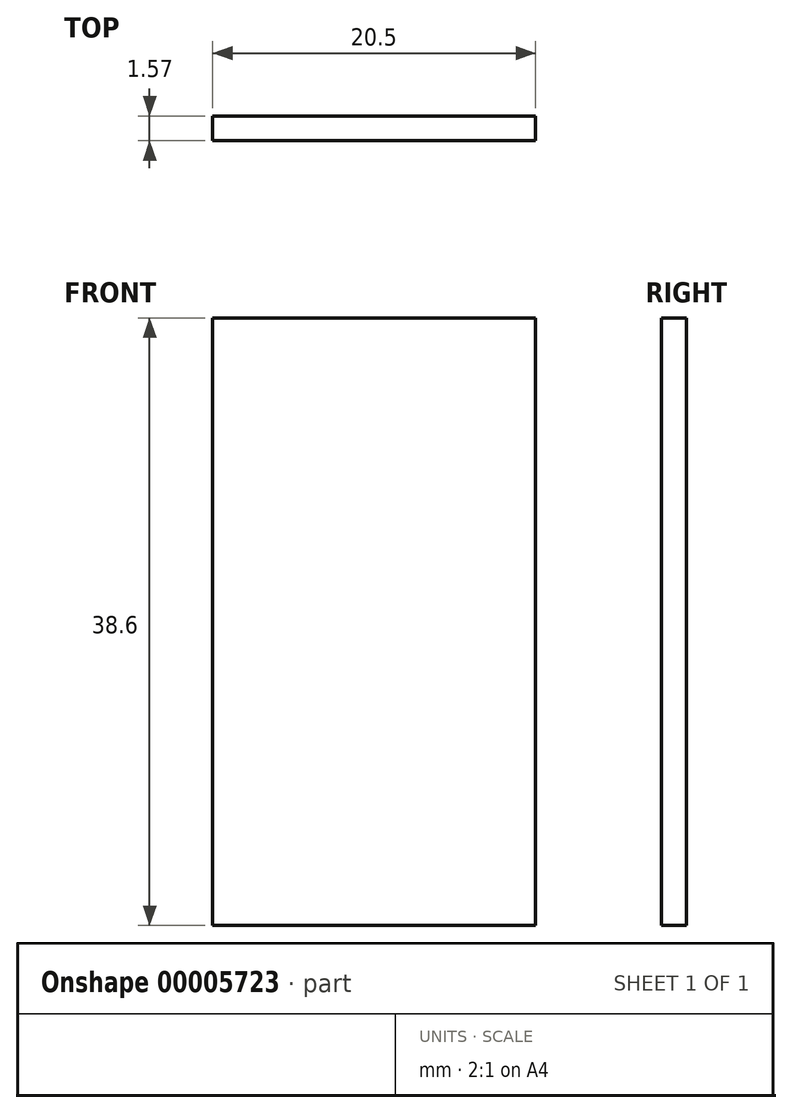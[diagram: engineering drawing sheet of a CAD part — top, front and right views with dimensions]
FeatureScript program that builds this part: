
annotation { "Feature Type Name" : "Feature", "Feature Type Description" : "" }
export const myFeature = defineFeature(function(context is Context, id is Id, definition is map)
    precondition{}
    {
        {
            var Q0;
            Q0=qCreatedBy(makeId("Front.planeOp"),FACE);
            var sketch = newSketch(context, id + "F0", { "sketchPlane" : qUnion([Q0])});
            skLineSegment(sketch, "E0.rect.bottom", {"start": v(10.25, 19.3) * mm, "end": v(-10.25, 19.3) * mm});
            skLineSegment(sketch, "E0.rect.top", {"start": v(10.25, -19.3) * mm, "end": v(-10.25, -19.3) * mm});
            skLineSegment(sketch, "E0.rect.left", {"start": v(10.25, 19.3) * mm, "end": v(10.25, -19.3) * mm});
            skLineSegment(sketch, "E0.rect.right", {"start": v(-10.25, 19.3) * mm, "end": v(-10.25, -19.3) * mm});
            skPoint(sketch, "E0.rect.middle", {"position": v(0, 0) * mm});
            skSolve(sketch);
        }
        {
            var Q0;
            Q0=makeQuery(id+"F0.imprint","IMPRINT",FACE,{"disambiguationData":[TD([[makeQuery(id+"F0.imprint","IMPRINT",EDGE,{"derivedFrom":sQuery(id+"F0.wireOp",EDGE,"E0.rect.bottom")}),1.0]])]});
            extrude(context, id + "F1", {"entities" : qUnion([Q0]), "depth" : 1.57 * mm});
        }
    });
